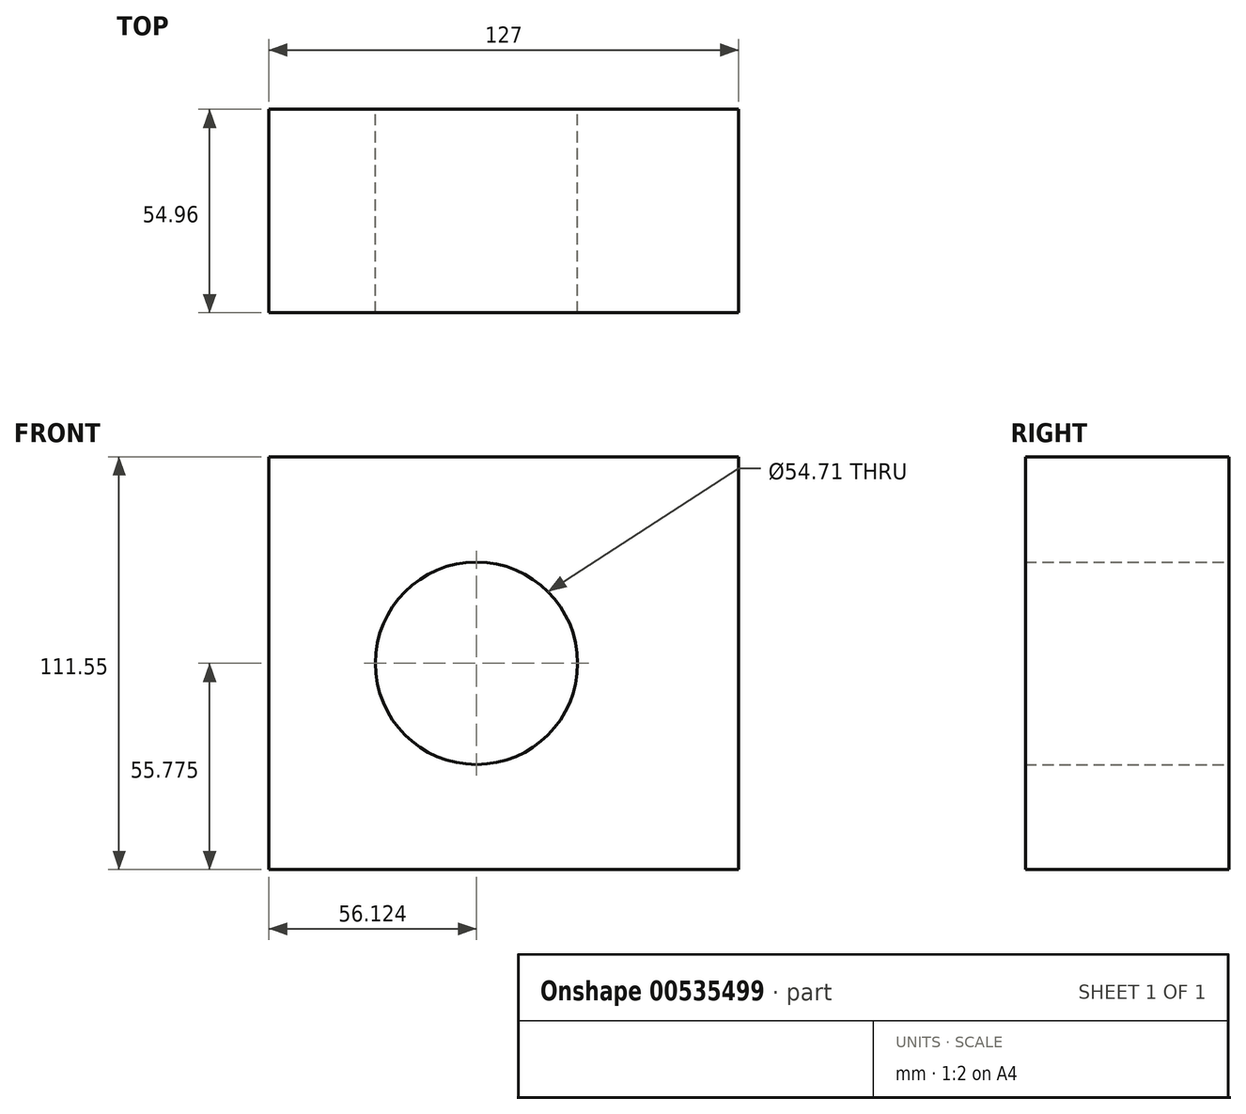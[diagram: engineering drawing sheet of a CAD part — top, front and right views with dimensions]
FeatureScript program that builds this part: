
annotation { "Feature Type Name" : "Feature", "Feature Type Description" : "" }
export const myFeature = defineFeature(function(context is Context, id is Id, definition is map)
    precondition{}
    {
        {
            var Q0;
            Q0=qCreatedBy(makeId("Right.planeOp"),FACE);
            var sketch = newSketch(context, id + "F0", { "sketchPlane" : qUnion([Q0])});
            skLineSegment(sketch, "E0.bottom", {"start": v(-54.96, 102.8) * mm, "end": v(0, 102.8) * mm});
            skLineSegment(sketch, "E0.top", {"start": v(-54.96, -8.76) * mm, "end": v(0, -8.76) * mm});
            skLineSegment(sketch, "E0.left", {"start": v(-54.96, 102.8) * mm, "end": v(-54.96, -8.76) * mm});
            skLineSegment(sketch, "E0.right", {"start": v(0, 102.8) * mm, "end": v(0, -8.76) * mm});
            skSolve(sketch);
        }
        {
            var Q0;
            Q0 = qSketchRegion(id + "F0", true);
            extrude(context, id + "F1", {"entities" : qUnion([Q0]), "depth" : 127 * mm, "offsetDistance" : 25.4 * mm});
        }
        {
            var Q0;
            Q0=makeQuery(id+"F1.opExtrude","SWEPT_FACE",FACE,{"disambiguationData":[OSD([sQuery(id+"F0.wireOp",EDGE,"E0.right")])]});
            var sketch = newSketch(context, id + "F2", { "sketchPlane" : qUnion([Q0])});
            skCircle(sketch, "E1", {"center": v(-56.12, 47.01) * mm, "radius": 27.36 * mm});
            skPoint(sketch, "E1.centerSnap0", {"position": v(0, 47.01) * mm});
            skSolve(sketch);
        }
        {
            var Q0;
            Q0=makeQuery(id+"F2.imprint","IMPRINT",FACE,{"disambiguationData":[TD([[makeQuery(id+"F2.imprint","IMPRINT",EDGE,{"derivedFrom":sQuery(id+"F2.wireOp",EDGE,"E1")}),1.0]])]});
            extrude(context, id + "F3", {"entities" : qUnion([Q0]), "operationType" : NewBodyOperationType.REMOVE, "depth" : -55.46 * mm, "offsetDistance" : 25.4 * mm});
        }
    });
